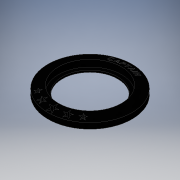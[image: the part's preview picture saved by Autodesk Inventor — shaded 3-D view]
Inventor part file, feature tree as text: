
AUTODESK INVENTOR PART (.ipt)
format: ipt  version: 2016 (Build 200138000, 138)  size: 496,128 bytes
history: native  units: in
note: dims shown in document units (in); Inventor stores cm internally (conversion verified against a paired STEP export)
features: sketch x2, revolve x1, extrude x1, projected_geometry x1
ambient origin geometry x8: Origin, YZ Plane, XZ Plane, XY Plane, X Axis, Y Axis, Z Axis, Center Point
bodies: Solid1 (feature_tree)
feature tree (5):
  revolve  "Revolution1"  [1 undecoded]
  extrude  "Extrusion1"  Depth=0.1in
  sketch  "Sketch1"  dims[d0=0.8265in d1=0.175in]
  sketch  "Sketch2"  dims[d2=0.05in d3=0.1in d4=0.15in d5=0.275in d6=90.0deg d7=0.075in d10=0.245in d11=0.1374in d12=0.1202in d13=1.95in d14=0.089in d15=0.074in d16=0.059in d17=0.0in d18=0.0in d19=0.074in d20=0.059in]
  projected_geometry  "Projected Loop1"
note: 1 required parameter value undecoded (feature->parameter linkage not recoverable at this tier; creation-order binding heuristic only, values carry confidence <= 0.55)
